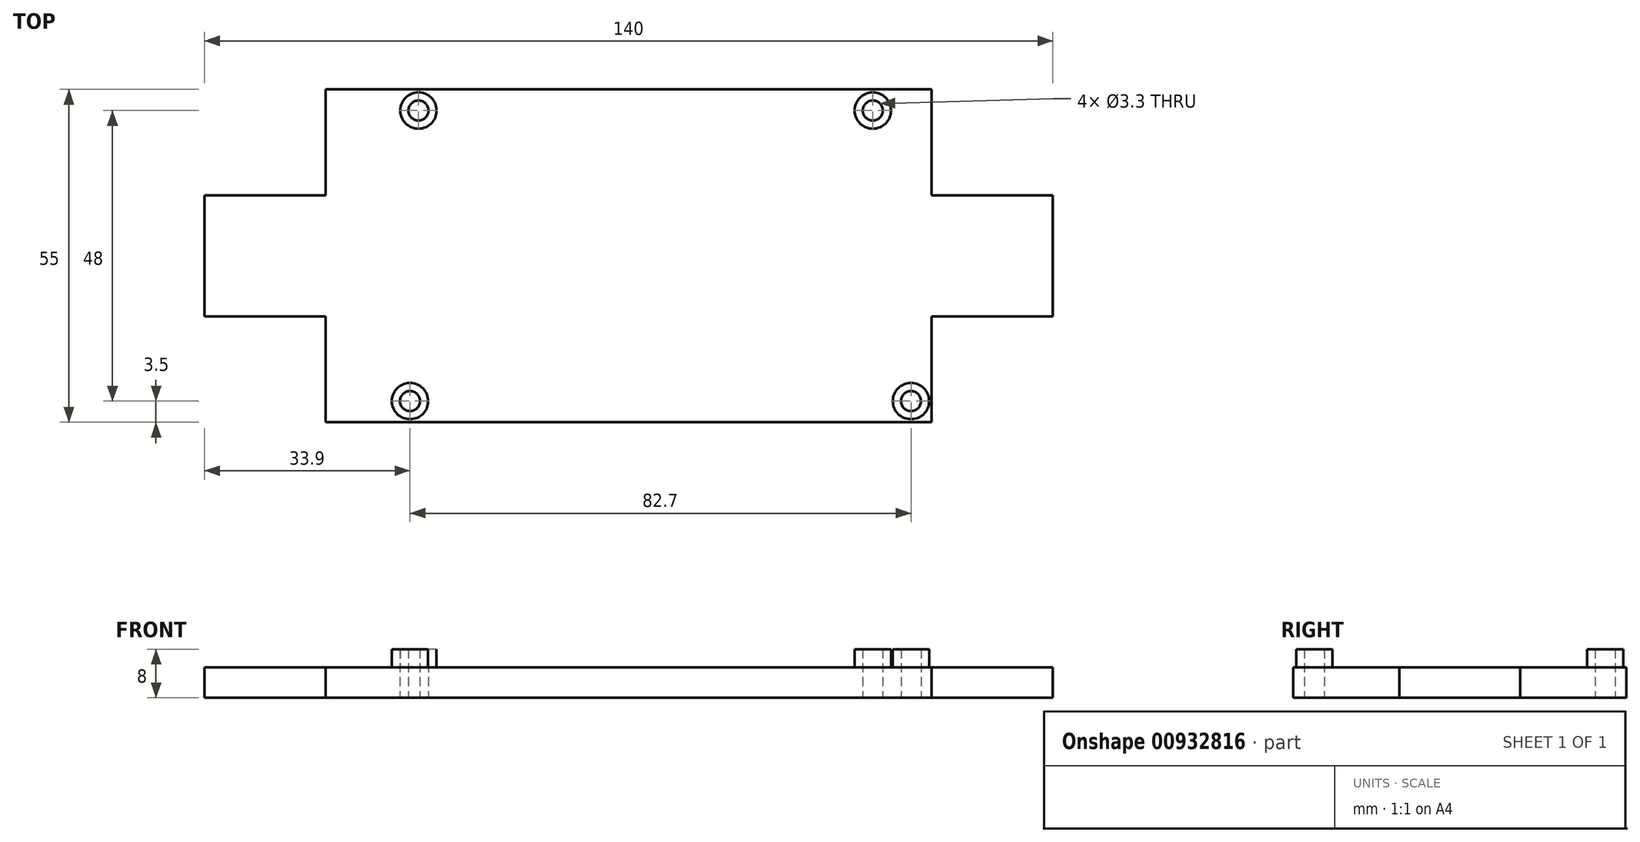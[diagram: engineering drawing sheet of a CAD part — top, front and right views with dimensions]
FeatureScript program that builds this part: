
annotation { "Feature Type Name" : "Feature", "Feature Type Description" : "" }
export const myFeature = defineFeature(function(context is Context, id is Id, definition is map)
    precondition{}
    {
        {
            var Q0;
            Q0=qCreatedBy(makeId("Top.planeOp"),FACE);
            var sketch = newSketch(context, id + "F0", { "sketchPlane" : qUnion([Q0])});
            skLineSegment(sketch, "E0.bottom", {"start": v(50, 27.5) * mm, "end": v(-50, 27.5) * mm});
            skLineSegment(sketch, "E0.top", {"start": v(50, -27.5) * mm, "end": v(-50, -27.5) * mm});
            skLineSegment(sketch, "E0.left", {"start": v(50, 27.5) * mm, "end": v(50, 10) * mm});
            skLineSegment(sketch, "E0.right", {"start": v(-50, 27.5) * mm, "end": v(-50, 10) * mm});
            skPoint(sketch, "E0.middle", {"position": v(0, 0) * mm});
            skLineSegment(sketch, "E1.bottom", {"start": v(-50, -10) * mm, "end": v(-70, -10) * mm});
            skLineSegment(sketch, "E1.top", {"start": v(-50, 10) * mm, "end": v(-70, 10) * mm});
            skLineSegment(sketch, "E1.right", {"start": v(-70, -10) * mm, "end": v(-70, 10) * mm});
            skLineSegment(sketch, "E2.trimOffspring", {"start": v(-50, -10) * mm, "end": v(-50, -27.5) * mm});
            skLineSegment(sketch, "E3.MirrorCS", {"start": v(50, 10) * mm, "end": v(70, 10) * mm});
            skLineSegment(sketch, "E4.MirrorCS", {"start": v(70, -10) * mm, "end": v(70, 10) * mm});
            skLineSegment(sketch, "E5.MirrorCS", {"start": v(50, -10) * mm, "end": v(70, -10) * mm});
            skLineSegment(sketch, "E6.trimOffspring", {"start": v(50, -10) * mm, "end": v(50, -27.5) * mm});
            skSolve(sketch);
        }
        {
            var Q0;
            Q0 = qSketchRegion(id + "F0", true);
            extrude(context, id + "F1", {"entities" : qUnion([Q0]), "depth" : 5 * mm, "offsetDistance" : 25 * mm});
        }
        {
            var Q0;
            Q0=makeQuery(id+"F1.opExtrude","CAP_FACE",FACE,{"disambiguationData":[OSD([sQuery(id+"F0.wireOp",EDGE,"E0.bottom"),sQuery(id+"F0.wireOp",EDGE,"E0.top"),sQuery(id+"F0.wireOp",EDGE,"E0.left"),sQuery(id+"F0.wireOp",EDGE,"E0.right")])],"isStart":false});
            var sketch = newSketch(context, id + "F2", { "sketchPlane" : qUnion([Q0])});
            skCircle(sketch, "E7", {"center": v(-34.7, 24) * mm, "radius": 1.65 * mm});
            skCircle(sketch, "E8", {"center": v(40.3, 24) * mm, "radius": 1.65 * mm});
            skCircle(sketch, "E9", {"center": v(-36.1, -24) * mm, "radius": 1.65 * mm});
            skCircle(sketch, "E10", {"center": v(46.6, -24) * mm, "radius": 1.65 * mm});
            skSolve(sketch);
        }
        {
            var Q0;
            Q0 = qSketchRegion(id + "F2", true);
            extrude(context, id + "F3", {"entities" : qUnion([Q0]), "operationType" : NewBodyOperationType.REMOVE, "endBound" : BoundingType.SYMMETRIC, "depth" : 37.6 * mm, "offsetDistance" : 25 * mm});
        }
        {
            var Q0;
            Q0=makeQuery(id+"F1.opExtrude","CAP_FACE",FACE,{"disambiguationData":[OSD([sQuery(id+"F0.wireOp",EDGE,"E0.bottom"),sQuery(id+"F0.wireOp",EDGE,"E0.top"),sQuery(id+"F0.wireOp",EDGE,"E0.left"),sQuery(id+"F0.wireOp",EDGE,"E0.right")])],"isStart":false});
            var sketch = newSketch(context, id + "F4", { "sketchPlane" : qUnion([Q0])});
            skCircle(sketch, "E11", {"center": v(-34.7, 24) * mm, "radius": 3 * mm});
            skCircle(sketch, "E12", {"center": v(40.3, 24) * mm, "radius": 3 * mm});
            skCircle(sketch, "E13", {"center": v(46.6, -24) * mm, "radius": 3 * mm});
            skCircle(sketch, "E14", {"center": v(-36.1, -24) * mm, "radius": 3 * mm});
            skSolve(sketch);
        }
        {
            var Q0;
            Q0 = qSketchRegion(id + "F4", true);
            extrude(context, id + "F5", {"entities" : qUnion([Q0]), "operationType" : NewBodyOperationType.ADD, "depth" : 3 * mm, "offsetDistance" : 25 * mm});
        }
        {
            var Q0;
            Q0 = qSketchRegion(id + "F2", true);
            extrude(context, id + "F6", {"entities" : qUnion([Q0]), "operationType" : NewBodyOperationType.REMOVE, "depth" : 25 * mm, "offsetDistance" : 25 * mm});
        }
    });
